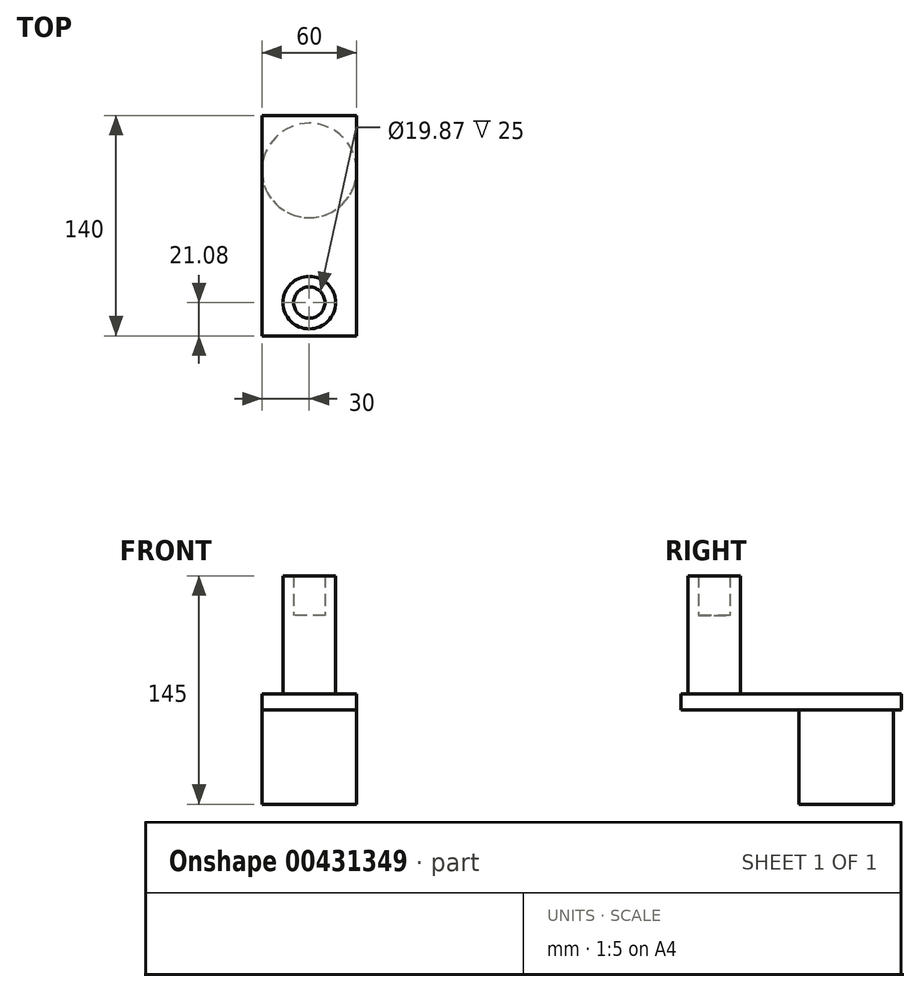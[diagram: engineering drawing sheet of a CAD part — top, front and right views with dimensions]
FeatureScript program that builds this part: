
annotation { "Feature Type Name" : "Feature", "Feature Type Description" : "" }
export const myFeature = defineFeature(function(context is Context, id is Id, definition is map)
    precondition{}
    {
        {
            var Q0;
            Q0=qCreatedBy(makeId("Top.planeOp"),FACE);
            var sketch = newSketch(context, id + "F0", { "sketchPlane" : qUnion([Q0])});
            skCircle(sketch, "E0", {"center": v(0, 0) * mm, "radius": 30 * mm});
            skSolve(sketch);
        }
        {
            var Q0;
            Q0=makeQuery(id+"F0.imprint","IMPRINT",FACE,{"disambiguationData":[TD([[makeQuery(id+"F0.imprint","IMPRINT",EDGE,{"derivedFrom":sQuery(id+"F0.wireOp",EDGE,"E0")}),1.0]])]});
            extrude(context, id + "F1", {"entities" : qUnion([Q0]), "depth" : 60 * mm});
        }
        {
            var Q0;
            Q0=makeQuery(id+"F1.opExtrude","CAP_FACE",FACE,{"disambiguationData":[OSD([sQuery(id+"F0.wireOp",EDGE,"E0")])],"isStart":false});
            var sketch = newSketch(context, id + "F2", { "sketchPlane" : qUnion([Q0])});
            skLineSegment(sketch, "E1.bottom", {"start": v(-30, 35) * mm, "end": v(30, 35) * mm});
            skLineSegment(sketch, "E1.top", {"start": v(-30, -105) * mm, "end": v(30, -105) * mm});
            skLineSegment(sketch, "E1.left", {"start": v(-30, 35) * mm, "end": v(-30, -105) * mm});
            skLineSegment(sketch, "E1.right", {"start": v(30, 35) * mm, "end": v(30, -105) * mm});
            skSolve(sketch);
        }
        {
            var Q0;
            Q0 = qSketchRegion(id + "F2", true);
            extrude(context, id + "F3", {"entities" : qUnion([Q0]), "operationType" : NewBodyOperationType.ADD, "depth" : 10 * mm});
        }
        {
            var Q0;
            Q0=makeQuery(id+"F3.opExtrude","CAP_FACE",FACE,{"disambiguationData":[OSD([sQuery(id+"F2.wireOp",EDGE,"E1.bottom"),sQuery(id+"F2.wireOp",EDGE,"E1.top"),sQuery(id+"F2.wireOp",EDGE,"E1.left"),sQuery(id+"F2.wireOp",EDGE,"E1.right")])],"isStart":false});
            var sketch = newSketch(context, id + "F4", { "sketchPlane" : qUnion([Q0])});
            skCircle(sketch, "E2", {"center": v(0, -83.92) * mm, "radius": 16.7 * mm});
            skSolve(sketch);
        }
        {
            var Q0;
            Q0=makeQuery(id+"F4.imprint","IMPRINT",FACE,{"disambiguationData":[TD([[makeQuery(id+"F4.imprint","IMPRINT",EDGE,{"derivedFrom":sQuery(id+"F4.wireOp",EDGE,"E2")}),1.0]])]});
            extrude(context, id + "F5", {"entities" : qUnion([Q0]), "operationType" : NewBodyOperationType.ADD, "depth" : 50 * mm});
        }
        {
            var Q0;
            Q0=makeQuery(id+"F5.opExtrude","CAP_FACE",FACE,{"disambiguationData":[OSD([sQuery(id+"F4.wireOp",EDGE,"E2")])],"isStart":false});
            var sketch = newSketch(context, id + "F6", { "sketchPlane" : qUnion([Q0])});
            skCircle(sketch, "E3", {"center": v(0, -83.92) * mm, "radius": 9.93 * mm});
            skSolve(sketch);
        }
        {
            var Q0;
            Q0=makeQuery(id+"F6.imprint","IMPRINT",FACE,{"disambiguationData":[TD([[makeQuery(id+"F6.imprint","IMPRINT",EDGE,{"derivedFrom":sQuery(id+"F6.wireOp",EDGE,"E3")}),-1.0]])]});
            extrude(context, id + "F7", {"entities" : qUnion([Q0]), "operationType" : NewBodyOperationType.ADD, "depth" : 25 * mm});
        }
    });
